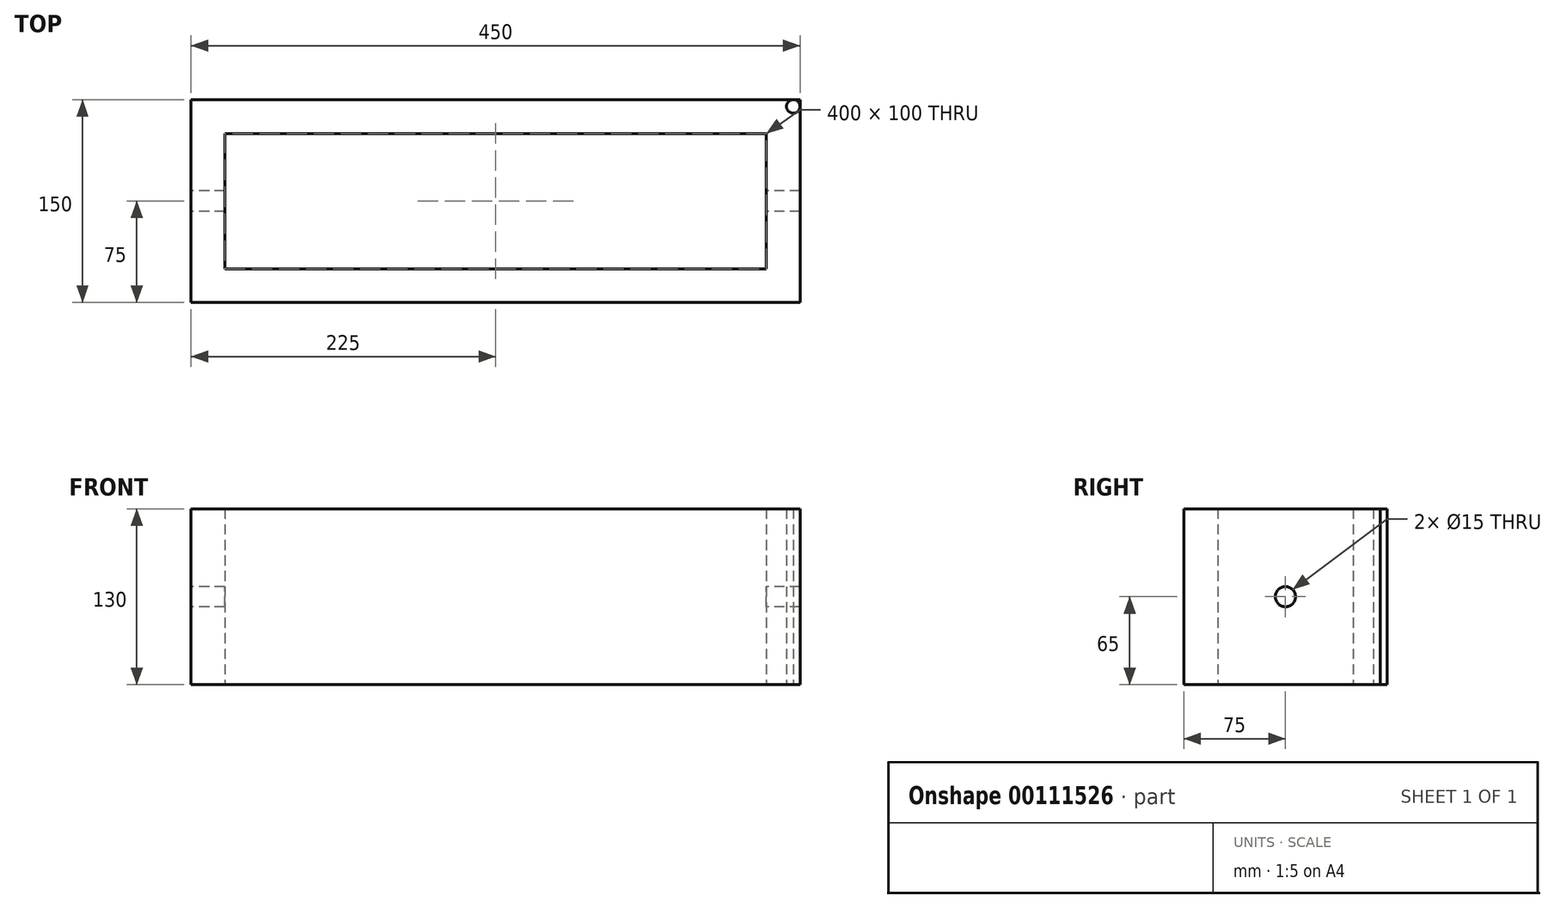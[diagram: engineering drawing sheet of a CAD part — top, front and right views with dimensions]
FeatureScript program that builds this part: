
annotation { "Feature Type Name" : "Feature", "Feature Type Description" : "" }
export const myFeature = defineFeature(function(context is Context, id is Id, definition is map)
    precondition{}
    {
        {
            var Q0;
            Q0=qCreatedBy(makeId("Top.planeOp"),FACE);
            var sketch = newSketch(context, id + "F0", { "sketchPlane" : qUnion([Q0])});
            skLineSegment(sketch, "E0.bottom", {"start": v(-225, 75) * mm, "end": v(225, 75) * mm});
            skLineSegment(sketch, "E0.top", {"start": v(-225, -75) * mm, "end": v(225, -75) * mm});
            skLineSegment(sketch, "E0.left", {"start": v(-225, 75) * mm, "end": v(-225, -75) * mm});
            skLineSegment(sketch, "E0.right", {"start": v(225, 75) * mm, "end": v(225, -75) * mm});
            skPoint(sketch, "E0.middle", {"position": v(0, 0) * mm});
            skLineSegment(sketch, "E1.bottom", {"start": v(-200, 50) * mm, "end": v(200, 50) * mm});
            skLineSegment(sketch, "E1.top", {"start": v(-200, -50) * mm, "end": v(200, -50) * mm});
            skLineSegment(sketch, "E1.left", {"start": v(-200, 50) * mm, "end": v(-200, -50) * mm});
            skLineSegment(sketch, "E1.right", {"start": v(200, 50) * mm, "end": v(200, -50) * mm});
            skPoint(sketch, "E2", {"position": v(220, 70) * mm});
            skCircle(sketch, "E3", {"center": v(220, 70) * mm, "radius": 5 * mm});
            skSolve(sketch);
        }
        {
            var Q0;
            Q0=makeQuery(id+"F0.imprint","IMPRINT",FACE,{"disambiguationData":[TD([[makeQuery(id+"F0.imprint","IMPRINT",EDGE,{"derivedFrom":sQuery(id+"F0.wireOp",EDGE,"E0.bottom")}),-1.0]])]});
            var Q1;
            {var subQ1=sQuery(id+"F0.wireOp",EDGE,"E0.top");Q1=makeQuery(id+"F0.imprint","IMPRINT",FACE,{"disambiguationData":[TD([[makeQuery(id+"F0.imprint","IMPRINT",EDGE,{"derivedFrom":subQ1}),1.0]])]});}
            extrude(context, id + "F1", {"entities" : qUnion([Q0, Q1]), "endBound" : BoundingType.SYMMETRIC, "depth" : 130 * mm});
        }
        {
            var Q0;
            Q0=makeQuery(id+"F1.opExtrude","SWEPT_FACE",FACE,{"disambiguationData":[OSD([sQuery(id+"F0.wireOp",EDGE,"E0.left")])]});
            var sketch = newSketch(context, id + "F2", { "sketchPlane" : qUnion([Q0])});
            skCircle(sketch, "E4", {"center": v(0, 0) * mm, "radius": 7.5 * mm});
            skSolve(sketch);
        }
        {
            var Q0;
            Q0=makeQuery(id+"F2.imprint","IMPRINT",FACE,{"disambiguationData":[TD([[makeQuery(id+"F2.imprint","IMPRINT",EDGE,{"derivedFrom":sQuery(id+"F2.wireOp",EDGE,"E4")}),1.0]])]});
            extrude(context, id + "F3", {"entities" : qUnion([Q0]), "operationType" : NewBodyOperationType.REMOVE, "endBound" : BoundingType.SYMMETRIC, "oppositeDirection" : true, "depth" : 1000 * mm});
        }
    });
